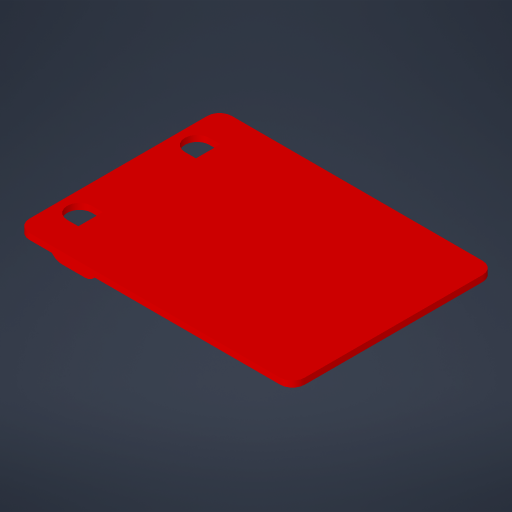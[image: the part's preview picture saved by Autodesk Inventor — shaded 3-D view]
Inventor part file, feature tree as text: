
AUTODESK INVENTOR PART (.ipt)
format: ipt  version: 2023.4 (Build 274418000, 418)  size: 363,520 bytes
history: native  units: mm
features: reference x7, sketch x3, extrude x3, projected_geometry x2, other x2, plane x1, chamfer x1, fillet x1
ambient origin geometry x8: Origin, YZ Plane, XZ Plane, XY Plane, X Axis, Y Axis, Z Axis, Center Point
bodies: Solid1 (feature_tree)
feature tree (20):
  sketch  "Sketch1"  dims[d0=0.125mm d1=0.125mm]
  plane  "Work Plane1"
  extrude  "Extrusion1"  Depth=0.125mm
  extrude  "Extrusion2"  Depth=2.5mm
  extrude  "Extrusion3"  Depth=2.5mm
  chamfer  "Chamfer1"  Distance=1.25mm
  fillet  "Fillet1"  Radius=5.0mm
  reference  "Reference1"
  reference  "Reference2"
  reference  "Reference3"
  reference  "Reference4"
  sketch  "Sketch2"  dims[d2=0.125mm d3=2.5mm]
  reference  "Reference5"
  reference  "Reference6"
  reference  "Reference7"
  projected_geometry  "Projected Loop1"
  sketch  "Sketch3"  dims[d4=1.0mm d5=0.0mm d6=0.125mm d7=1.25mm d8=0.0mm d9=5.0mm d10=5.0mm d11=2.5mm d12=0.0mm d13=1.0mm d14=2.0mm d15=45.0deg d16=2.5mm]
  projected_geometry  "Projected Loop2"
  other  "XYZ Stage V5.iam"
  other  "Z Stage Body V5:1"
